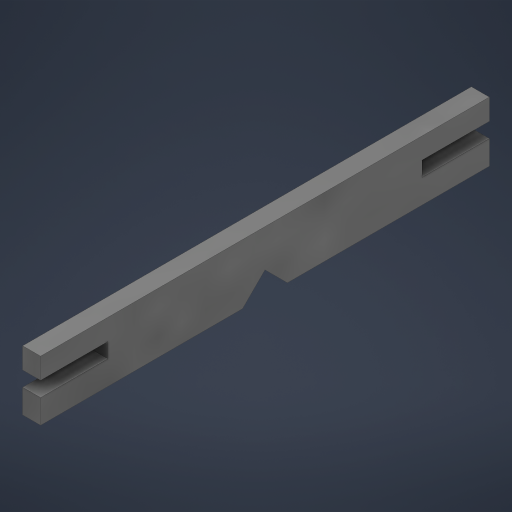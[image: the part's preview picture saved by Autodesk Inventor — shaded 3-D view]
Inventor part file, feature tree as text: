
AUTODESK INVENTOR PART (.ipt)
format: ipt  version: 2024 (Build 280153000, 153)  size: 260,608 bytes
history: native  units: in
note: dims shown in document units (in); Inventor stores cm internally (conversion verified against a paired STEP export)
features: extrude x3, sketch x1
ambient origin geometry x8: Origin, YZ Plane, XZ Plane, XY Plane, X Axis, Y Axis, Z Axis, Center Point
bodies: Solid1 (feature_tree)
feature tree (4):
  extrude  "Extrusion1"  Depth=0.5906in
  extrude  "Extrusion2"  Depth=0.0236in TaperAngle=0.0deg
  extrude  "Extrusion3"  Depth=0.0197in
  sketch  "Sketch2"  dims[d0=0.0787in d1=0.5906in d2=0.0236in d3=0.0in d4=0.0197in d7=0.0236in d8=0.0in d9=0.0276in d10=45.0deg d11=45.0deg d12=0.0591in d13=0.0236in d14=0.0in d15=0.4134in]
